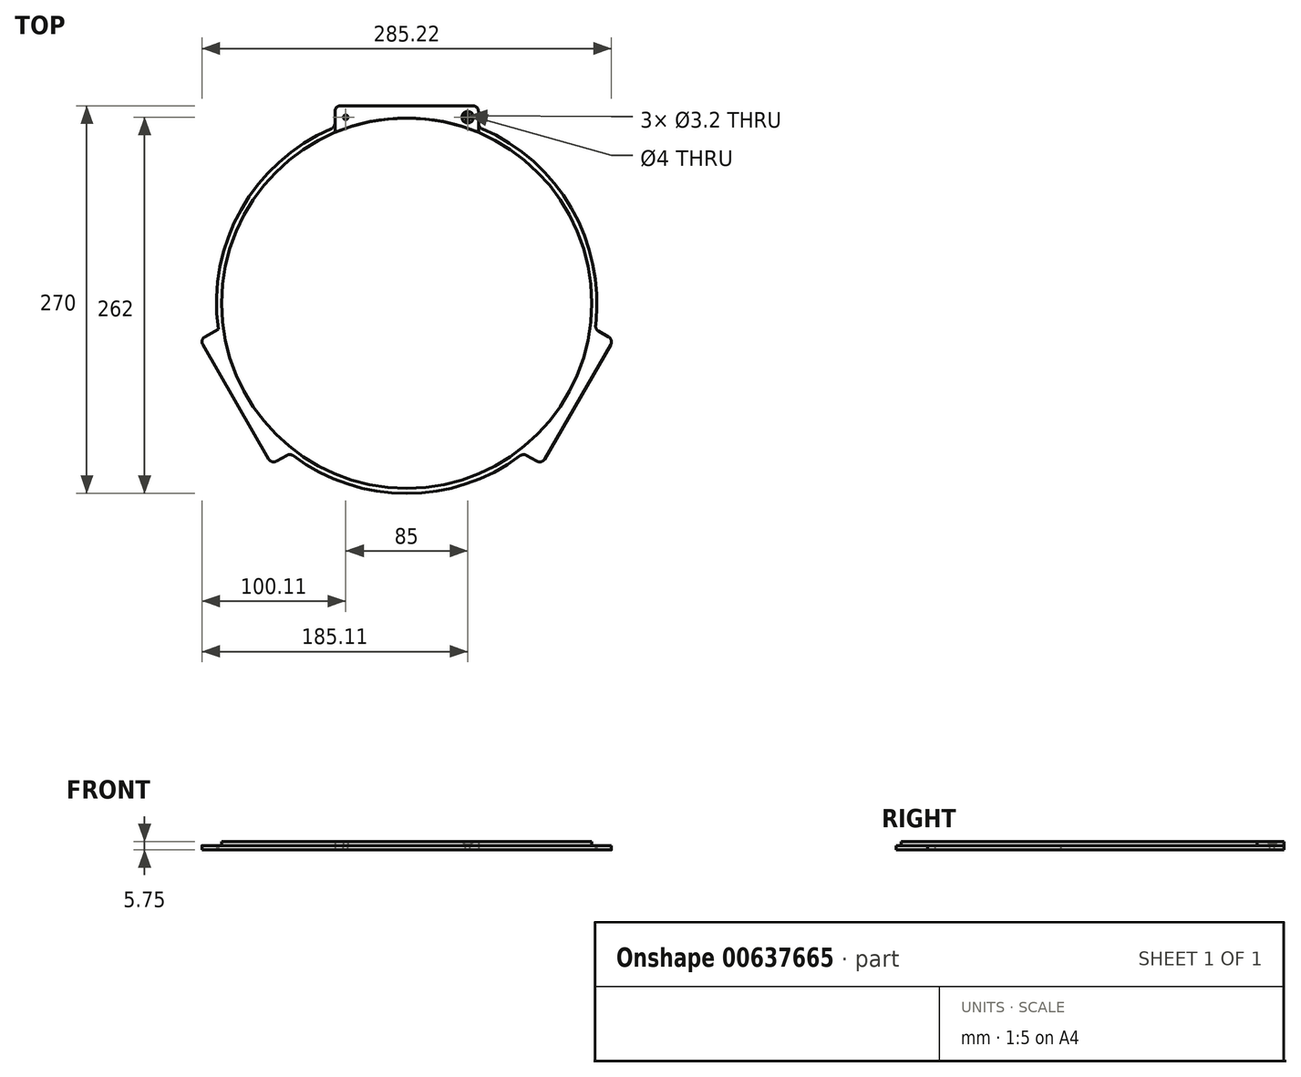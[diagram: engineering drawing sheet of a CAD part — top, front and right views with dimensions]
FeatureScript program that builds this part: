
annotation { "Feature Type Name" : "Feature", "Feature Type Description" : "" }
export const myFeature = defineFeature(function(context is Context, id is Id, definition is map)
    precondition{}
    {
        {
            var Q0;
            Q0=qCreatedBy(makeId("Front.planeOp"),FACE);
            var sketch = newSketch(context, id + "F0", { "sketchPlane" : qUnion([Q0])});
            skLineSegment(sketch, "E0", {"start": v(0, 73.34) * mm, "end": v(0, -75.96) * mm, "construction": true});
            skSolve(sketch);
        }
        {
            var Q0;
            Q0=qCreatedBy(makeId("Top.planeOp"),FACE);
            var sketch = newSketch(context, id + "F1", { "sketchPlane" : qUnion([Q0])});
            skArc(sketch, "E1", {"start": v(-79.18, -106.24) * mm, "mid": v(0, -132.5) * mm, "end": v(79.18, -106.24) * mm});
            skLineSegment(sketch, "E2", {"start": v(0, -132.5) * mm, "end": v(0, 137.5) * mm, "construction": true});
            skLineSegment(sketch, "E3", {"start": v(-46, 137.5) * mm, "end": v(46, 137.5) * mm});
            skLineSegment(sketch, "E4", {"start": v(50, 133.5) * mm, "end": v(50, 125.36) * mm});
            skLineSegment(sketch, "E5", {"start": v(-50, 133.5) * mm, "end": v(-50, 125.36) * mm});
            skLineSegment(sketch, "E6.1.0", {"start": v(-140.61, -23.45) * mm, "end": v(-131.26, -18.05) * mm});
            skLineSegment(sketch, "E6.1.1", {"start": v(-96.08, -108.59) * mm, "end": v(-142.08, -28.91) * mm});
            skLineSegment(sketch, "E6.1.7", {"start": v(-90.61, -110.05) * mm, "end": v(-83.57, -105.98) * mm});
            skLineSegment(sketch, "E6.2.0", {"start": v(90.61, -110.05) * mm, "end": v(83.57, -105.98) * mm});
            skLineSegment(sketch, "E6.2.1", {"start": v(142.08, -28.91) * mm, "end": v(96.08, -108.59) * mm});
            skLineSegment(sketch, "E6.2.7", {"start": v(140.61, -23.45) * mm, "end": v(133.57, -19.38) * mm});
            skPoint(sketch, "E7.visualSharp", {"position": v(-144.08, -25.45) * mm});
            skArc(sketch, "E7.filletArc", {"start": v(-140.61, -23.45) * mm, "mid": v(-142.48, -25.88) * mm, "end": v(-142.08, -28.91) * mm});
            skPoint(sketch, "E8.orphan", {"position": v(-131.26, -18.05) * mm});
            skPoint(sketch, "E9.orphan", {"position": v(-81.26, -104.65) * mm});
            skArc(sketch, "E10.trimOffspring", {"start": v(131.6, -15.45) * mm, "mid": v(114.75, 66.25) * mm, "end": v(52.42, 121.7) * mm});
            skArc(sketch, "E11.trimOffspring", {"start": v(-52.42, 121.7) * mm, "mid": v(-115.4, 65.11) * mm, "end": v(-131.26, -18.05) * mm});
            skPoint(sketch, "E12.visualSharp", {"position": v(-50, 122.7) * mm});
            skArc(sketch, "E12.filletArc", {"start": v(-52.42, 121.7) * mm, "mid": v(-50.66, 123.17) * mm, "end": v(-50, 125.36) * mm});
            skPoint(sketch, "E13.visualSharp", {"position": v(-50, 137.5) * mm});
            skArc(sketch, "E13.filletArc", {"start": v(-46, 137.5) * mm, "mid": v(-48.83, 136.33) * mm, "end": v(-50, 133.5) * mm});
            skPoint(sketch, "E14.visualSharp", {"position": v(50, 137.5) * mm});
            skArc(sketch, "E14.filletArc", {"start": v(50, 133.5) * mm, "mid": v(48.83, 136.33) * mm, "end": v(46, 137.5) * mm});
            skPoint(sketch, "E15.visualSharp", {"position": v(50, 122.7) * mm});
            skArc(sketch, "E15.filletArc", {"start": v(50, 125.36) * mm, "mid": v(50.66, 123.17) * mm, "end": v(52.42, 121.7) * mm});
            skPoint(sketch, "E16.visualSharp", {"position": v(131.26, -18.05) * mm});
            skArc(sketch, "E16.filletArc", {"start": v(131.6, -15.45) * mm, "mid": v(132, -17.71) * mm, "end": v(133.57, -19.38) * mm});
            skPoint(sketch, "E17.visualSharp", {"position": v(144.08, -25.45) * mm});
            skArc(sketch, "E17.filletArc", {"start": v(142.08, -28.91) * mm, "mid": v(142.48, -25.88) * mm, "end": v(140.61, -23.45) * mm});
            skPoint(sketch, "E18.visualSharp", {"position": v(94.08, -112.05) * mm});
            skArc(sketch, "E18.filletArc", {"start": v(90.61, -110.05) * mm, "mid": v(93.65, -110.45) * mm, "end": v(96.08, -108.59) * mm});
            skPoint(sketch, "E19.visualSharp", {"position": v(81.26, -104.65) * mm});
            skArc(sketch, "E19.filletArc", {"start": v(83.57, -105.98) * mm, "mid": v(81.34, -105.45) * mm, "end": v(79.18, -106.24) * mm});
            skArc(sketch, "E20.filletArc", {"start": v(-79.18, -106.24) * mm, "mid": v(-81.34, -105.45) * mm, "end": v(-83.57, -105.98) * mm});
            skPoint(sketch, "E21.visualSharp", {"position": v(-94.08, -112.05) * mm});
            skArc(sketch, "E21.filletArc", {"start": v(-96.08, -108.59) * mm, "mid": v(-93.65, -110.45) * mm, "end": v(-90.61, -110.05) * mm});
            skPoint(sketch, "E22", {"position": v(-42.5, 129.5) * mm});
            skPoint(sketch, "E23", {"position": v(42.5, 129.5) * mm});
            skSolve(sketch);
        }
        {
            var Q0;
            Q0=makeQuery(id+"F1.imprint","IMPRINT",FACE,{"disambiguationData":[TD([[makeQuery(id+"F1.imprint","IMPRINT",EDGE,{"derivedFrom":sQuery(id+"F1.wireOp",EDGE,"E1")}),1.0]])]});
            extrude(context, id + "F2", {"entities" : qUnion([Q0]), "depth" : 2.95 * mm, "offsetDistance" : 25 * mm});
        }
        {
            var Q0;
            Q0=sQuery(id+"F1.wireOp",VERTEX,"E22");
            var Q1;
            Q1=sQuery(id+"F1.wireOp",VERTEX,"E23");
            var Q2;
            Q2=sQuery(id+"F1.wireOp",VERTEX,"E6.2.6");
            var Q3;
            Q3=sQuery(id+"F1.wireOp",VERTEX,"E6.2.4");
            var Q4;
            Q4=sQuery(id+"F1.wireOp",VERTEX,"E6.1.6");
            var Q5;
            Q5=sQuery(id+"F1.wireOp",VERTEX,"E6.1.4");
            var Q6;
            Q6=makeQuery(id+"F2.opExtrude","SWEPT_BODY",BODY,{"disambiguationData":[OSD([sQuery(id+"F1.wireOp",EDGE,"E1"),sQuery(id+"F1.wireOp",EDGE,"E3"),sQuery(id+"F1.wireOp",EDGE,"E4"),sQuery(id+"F1.wireOp",EDGE,"E5"),sQuery(id+"F1.wireOp",EDGE,"E6.1.0"),sQuery(id+"F1.wireOp",EDGE,"E6.1.1"),sQuery(id+"F1.wireOp",EDGE,"E6.1.7"),sQuery(id+"F1.wireOp",EDGE,"E6.2.0"),sQuery(id+"F1.wireOp",EDGE,"E6.2.1"),sQuery(id+"F1.wireOp",EDGE,"E6.2.7"),sQuery(id+"F1.wireOp",EDGE,"E7.filletArc"),sQuery(id+"F1.wireOp",EDGE,"E10.trimOffspring"),sQuery(id+"F1.wireOp",EDGE,"E11.trimOffspring"),sQuery(id+"F1.wireOp",EDGE,"E12.filletArc"),sQuery(id+"F1.wireOp",EDGE,"E13.filletArc"),sQuery(id+"F1.wireOp",EDGE,"E14.filletArc"),sQuery(id+"F1.wireOp",EDGE,"E15.filletArc"),sQuery(id+"F1.wireOp",EDGE,"E16.filletArc"),sQuery(id+"F1.wireOp",EDGE,"E17.filletArc"),sQuery(id+"F1.wireOp",EDGE,"E18.filletArc"),sQuery(id+"F1.wireOp",EDGE,"E19.filletArc"),sQuery(id+"F1.wireOp",EDGE,"E20.filletArc"),sQuery(id+"F1.wireOp",EDGE,"E21.filletArc")])]});
            hole(context, id + "F3", {"style" : HoleStyle.SIMPLE, "endStyle" : HoleEndStyle.THROUGH, "oppositeDirection" : true, "holeDiameter" : 3.2 * mm, "majorDiameter" : 5 * mm, "isTappedThrough" : true, "tappedDepth" : 12 * mm, "tapClearance" : 3, "locations" : qUnion([Q0, Q1, Q2, Q3, Q4, Q5]), "scope" : qUnion([Q6]), "startStyle" : HoleStartStyle.PART});
        }
        {
            var Q0;
            Q0=makeQuery(id+"F2.opExtrude","CAP_FACE",FACE,{"disambiguationData":[OSD([sQuery(id+"F1.wireOp",EDGE,"E1"),sQuery(id+"F1.wireOp",EDGE,"E3"),sQuery(id+"F1.wireOp",EDGE,"E4"),sQuery(id+"F1.wireOp",EDGE,"E5"),sQuery(id+"F1.wireOp",EDGE,"E6.1.0"),sQuery(id+"F1.wireOp",EDGE,"E6.1.1"),sQuery(id+"F1.wireOp",EDGE,"E6.1.7"),sQuery(id+"F1.wireOp",EDGE,"E6.2.0"),sQuery(id+"F1.wireOp",EDGE,"E6.2.1"),sQuery(id+"F1.wireOp",EDGE,"E6.2.7"),sQuery(id+"F1.wireOp",EDGE,"E7.filletArc"),sQuery(id+"F1.wireOp",EDGE,"E10.trimOffspring"),sQuery(id+"F1.wireOp",EDGE,"E11.trimOffspring"),sQuery(id+"F1.wireOp",EDGE,"E12.filletArc"),sQuery(id+"F1.wireOp",EDGE,"E13.filletArc"),sQuery(id+"F1.wireOp",EDGE,"E14.filletArc"),sQuery(id+"F1.wireOp",EDGE,"E15.filletArc"),sQuery(id+"F1.wireOp",EDGE,"E16.filletArc"),sQuery(id+"F1.wireOp",EDGE,"E17.filletArc"),sQuery(id+"F1.wireOp",EDGE,"E18.filletArc"),sQuery(id+"F1.wireOp",EDGE,"E19.filletArc"),sQuery(id+"F1.wireOp",EDGE,"E20.filletArc"),sQuery(id+"F1.wireOp",EDGE,"E21.filletArc")])],"isStart":false});
            var sketch = newSketch(context, id + "F4", { "sketchPlane" : qUnion([Q0])});
            skPoint(sketch, "E24.0", {"position": v(0, 0) * mm});
            skCircle(sketch, "E25", {"center": v(0, 0) * mm, "radius": 129 * mm});
            skSolve(sketch);
        }
        {
            var Q0;
            Q0=makeQuery(id+"F4.imprint","IMPRINT",FACE,{"disambiguationData":[TD([[makeQuery(id+"F4.imprint","IMPRINT",EDGE,{"derivedFrom":sQuery(id+"F4.wireOp",EDGE,"E25")}),1.0]])]});
            extrude(context, id + "F5", {"entities" : qUnion([Q0]), "depth" : 2.8 * mm, "offsetDistance" : 25 * mm});
        }
        {
            var Q0;
            Q0=makeQuery(id+"F2.opExtrude","CAP_FACE",FACE,{"disambiguationData":[OSD([sQuery(id+"F1.wireOp",EDGE,"E1"),sQuery(id+"F1.wireOp",EDGE,"E3"),sQuery(id+"F1.wireOp",EDGE,"E4"),sQuery(id+"F1.wireOp",EDGE,"E5"),sQuery(id+"F1.wireOp",EDGE,"E6.1.0"),sQuery(id+"F1.wireOp",EDGE,"E6.1.1"),sQuery(id+"F1.wireOp",EDGE,"E6.1.7"),sQuery(id+"F1.wireOp",EDGE,"E6.2.0"),sQuery(id+"F1.wireOp",EDGE,"E6.2.1"),sQuery(id+"F1.wireOp",EDGE,"E6.2.7"),sQuery(id+"F1.wireOp",EDGE,"E7.filletArc"),sQuery(id+"F1.wireOp",EDGE,"E10.trimOffspring"),sQuery(id+"F1.wireOp",EDGE,"E11.trimOffspring"),sQuery(id+"F1.wireOp",EDGE,"E12.filletArc"),sQuery(id+"F1.wireOp",EDGE,"E13.filletArc"),sQuery(id+"F1.wireOp",EDGE,"E14.filletArc"),sQuery(id+"F1.wireOp",EDGE,"E15.filletArc"),sQuery(id+"F1.wireOp",EDGE,"E16.filletArc"),sQuery(id+"F1.wireOp",EDGE,"E17.filletArc"),sQuery(id+"F1.wireOp",EDGE,"E18.filletArc"),sQuery(id+"F1.wireOp",EDGE,"E19.filletArc"),sQuery(id+"F1.wireOp",EDGE,"E20.filletArc"),sQuery(id+"F1.wireOp",EDGE,"E21.filletArc")])],"isStart":false});
            var sketch = newSketch(context, id + "F6", { "sketchPlane" : qUnion([Q0])});
            skLineSegment(sketch, "E26.0", {"start": v(-50, 133.5) * mm, "end": v(-50, 118.92) * mm});
            skArc(sketch, "E27.0", {"start": v(-46, 137.5) * mm, "mid": v(-48.83, 136.33) * mm, "end": v(-50, 133.5) * mm});
            skLineSegment(sketch, "E28.0", {"start": v(-46, 137.5) * mm, "end": v(46, 137.5) * mm});
            skCircle(sketch, "E29.0", {"center": v(135.82, -28.76) * mm, "radius": 1.6 * mm, "construction": true});
            skPoint(sketch, "E30.orphan", {"position": v(-50, 125.36) * mm});
            skPoint(sketch, "E31.orphan", {"position": v(-71.84, 105.71) * mm});
            skArc(sketch, "E32.0", {"start": v(50, 133.5) * mm, "mid": v(48.83, 136.33) * mm, "end": v(46, 137.5) * mm});
            skLineSegment(sketch, "E33.0", {"start": v(50, 133.5) * mm, "end": v(50, 118.92) * mm});
            skArc(sketch, "E34.0", {"start": v(50, 118.92) * mm, "mid": v(0, 129) * mm, "end": v(-50, 118.92) * mm});
            skPoint(sketch, "E35.orphan", {"position": v(50, 125.36) * mm});
            skCircle(sketch, "E36.0", {"center": v(92.82, -103.24) * mm, "radius": 1.6 * mm, "construction": true});
            skSolve(sketch);
        }
        {
            var Q0;
            {var subQ0=sQuery(id+"F6.wireOp",EDGE,"E27.0");Q0=makeQuery(id+"F6.imprint","IMPRINT",FACE,{"disambiguationData":[TD([[makeQuery(id+"F6.imprint","IMPRINT",EDGE,{"derivedFrom":subQ0}),1.0]])]});}
            extrude(context, id + "F7", {"entities" : qUnion([Q0]), "depth" : 2.8 * mm, "offsetDistance" : 25 * mm});
        }
        {
            var Q0;
            Q0=makeQuery(id+"F7.opExtrude","CAP_FACE",FACE,{"disambiguationData":[OSD([sQuery(id+"F1.wireOp",EDGE,"E1"),sQuery(id+"F1.wireOp",EDGE,"E3"),sQuery(id+"F1.wireOp",EDGE,"E4"),sQuery(id+"F1.wireOp",EDGE,"E5"),sQuery(id+"F1.wireOp",EDGE,"E6.1.0"),sQuery(id+"F1.wireOp",EDGE,"E6.1.1"),sQuery(id+"F1.wireOp",EDGE,"E6.1.7"),sQuery(id+"F1.wireOp",EDGE,"E6.2.0"),sQuery(id+"F1.wireOp",EDGE,"E6.2.1"),sQuery(id+"F1.wireOp",EDGE,"E6.2.7"),sQuery(id+"F1.wireOp",EDGE,"E7.filletArc"),sQuery(id+"F1.wireOp",EDGE,"E10.trimOffspring"),sQuery(id+"F1.wireOp",EDGE,"E11.trimOffspring"),sQuery(id+"F1.wireOp",EDGE,"E12.filletArc"),sQuery(id+"F1.wireOp",EDGE,"E13.filletArc"),sQuery(id+"F1.wireOp",EDGE,"E14.filletArc"),sQuery(id+"F1.wireOp",EDGE,"E15.filletArc"),sQuery(id+"F1.wireOp",EDGE,"E16.filletArc"),sQuery(id+"F1.wireOp",EDGE,"E17.filletArc"),sQuery(id+"F1.wireOp",EDGE,"E18.filletArc"),sQuery(id+"F1.wireOp",EDGE,"E19.filletArc"),sQuery(id+"F1.wireOp",EDGE,"E20.filletArc"),sQuery(id+"F1.wireOp",EDGE,"E21.filletArc"),sQuery(id+"F3.hole-2.sketch.wireOp",EDGE,"core_line_2"),sQuery(id+"F3.hole-3.sketch.wireOp",EDGE,"core_line_2"),sQuery(id+"F6.wireOp",EDGE,"E26.0"),sQuery(id+"F6.wireOp",EDGE,"E27.0"),sQuery(id+"F6.wireOp",EDGE,"E28.0"),sQuery(id+"F6.wireOp",EDGE,"E32.0"),sQuery(id+"F6.wireOp",EDGE,"E33.0"),sQuery(id+"F6.wireOp",EDGE,"E34.0")])],"isStart":false});
            var sketch = newSketch(context, id + "F8", { "sketchPlane" : qUnion([Q0])});
            skCircle(sketch, "E37.0", {"center": v(-42.5, 129.5) * mm, "radius": 1.6 * mm, "construction": true});
            skCircle(sketch, "E38.0", {"center": v(42.5, 129.5) * mm, "radius": 1.6 * mm});
            skSolve(sketch);
        }
        {
            var Q0;
            Q0=sQuery(id+"F8.wireOp",VERTEX,"E38.0.center");
            var Q1;
            Q1=sQuery(id+"F8.wireOp",VERTEX,"E37.0.center");
            var Q2;
            Q2=makeQuery(id+"F7.opExtrude","SWEPT_BODY",BODY,{"disambiguationData":[OSD([sQuery(id+"F1.wireOp",EDGE,"E1"),sQuery(id+"F1.wireOp",EDGE,"E3"),sQuery(id+"F1.wireOp",EDGE,"E4"),sQuery(id+"F1.wireOp",EDGE,"E5"),sQuery(id+"F1.wireOp",EDGE,"E6.1.0"),sQuery(id+"F1.wireOp",EDGE,"E6.1.1"),sQuery(id+"F1.wireOp",EDGE,"E6.1.7"),sQuery(id+"F1.wireOp",EDGE,"E6.2.0"),sQuery(id+"F1.wireOp",EDGE,"E6.2.1"),sQuery(id+"F1.wireOp",EDGE,"E6.2.7"),sQuery(id+"F1.wireOp",EDGE,"E7.filletArc"),sQuery(id+"F1.wireOp",EDGE,"E10.trimOffspring"),sQuery(id+"F1.wireOp",EDGE,"E11.trimOffspring"),sQuery(id+"F1.wireOp",EDGE,"E12.filletArc"),sQuery(id+"F1.wireOp",EDGE,"E13.filletArc"),sQuery(id+"F1.wireOp",EDGE,"E14.filletArc"),sQuery(id+"F1.wireOp",EDGE,"E15.filletArc"),sQuery(id+"F1.wireOp",EDGE,"E16.filletArc"),sQuery(id+"F1.wireOp",EDGE,"E17.filletArc"),sQuery(id+"F1.wireOp",EDGE,"E18.filletArc"),sQuery(id+"F1.wireOp",EDGE,"E19.filletArc"),sQuery(id+"F1.wireOp",EDGE,"E20.filletArc"),sQuery(id+"F1.wireOp",EDGE,"E21.filletArc"),sQuery(id+"F3.hole-2.sketch.wireOp",EDGE,"core_line_2"),sQuery(id+"F3.hole-3.sketch.wireOp",EDGE,"core_line_2"),sQuery(id+"F6.wireOp",EDGE,"E26.0"),sQuery(id+"F6.wireOp",EDGE,"E27.0"),sQuery(id+"F6.wireOp",EDGE,"E28.0"),sQuery(id+"F6.wireOp",EDGE,"E32.0"),sQuery(id+"F6.wireOp",EDGE,"E33.0"),sQuery(id+"F6.wireOp",EDGE,"E34.0")])]});
            hole(context, id + "F9", {"style" : HoleStyle.C_SINK, "endStyle" : HoleEndStyle.THROUGH, "holeDiameter" : 4 * mm, "cSinkDiameter" : 8 * mm, "cSinkAngle" : 90 * degree, "majorDiameter" : 5 * mm, "isTappedThrough" : true, "tappedDepth" : 12 * mm, "tapClearance" : 3, "locations" : qUnion([Q0, Q1]), "scope" : qUnion([Q2]), "startStyle" : HoleStartStyle.PART});
        }
    });
